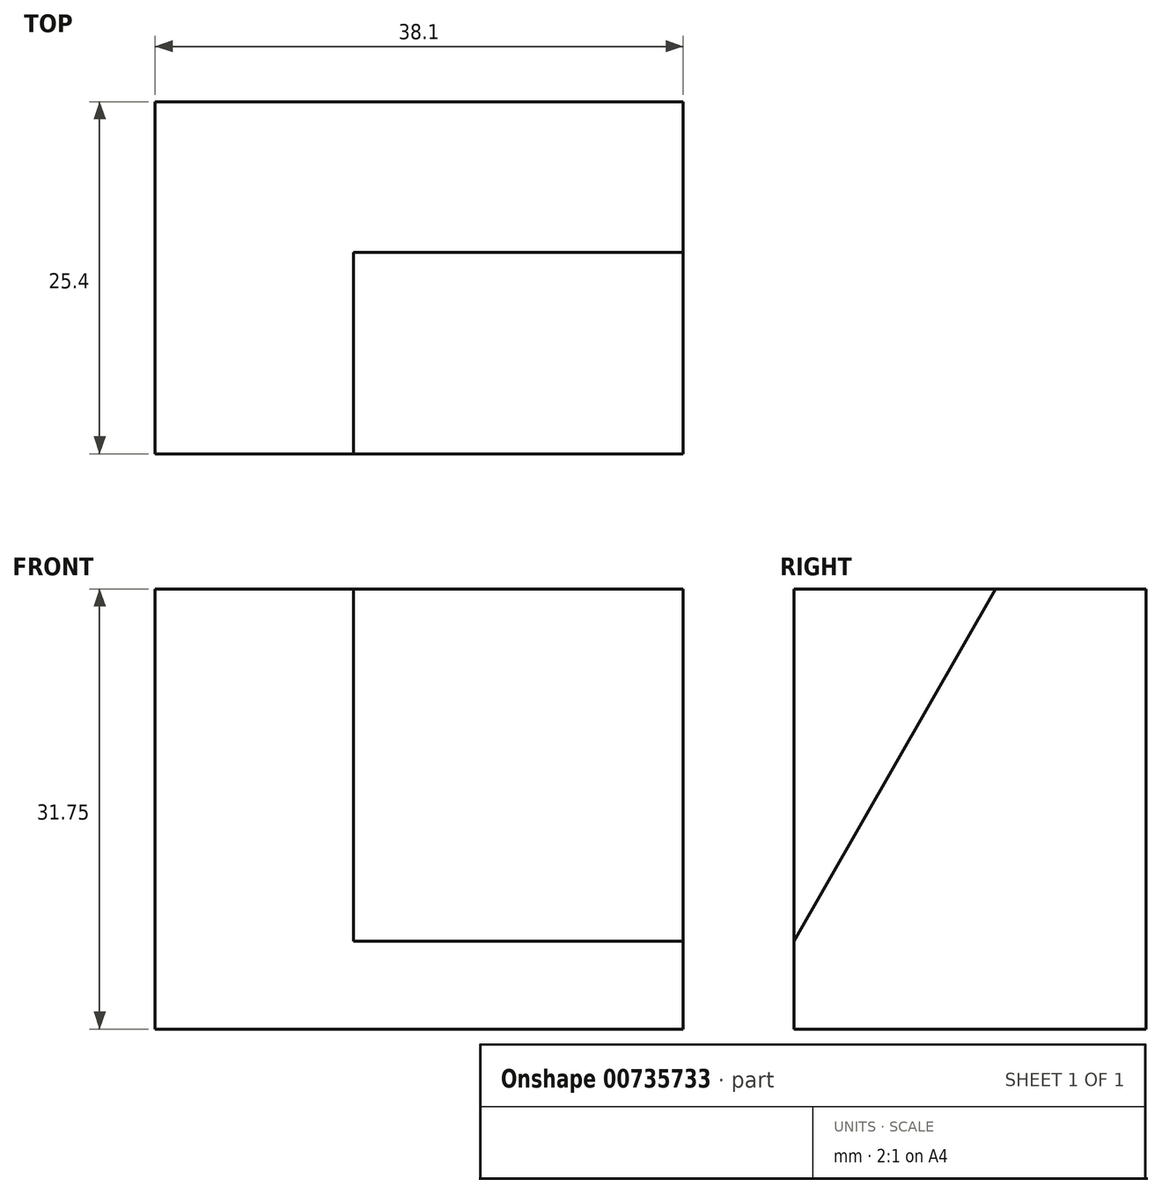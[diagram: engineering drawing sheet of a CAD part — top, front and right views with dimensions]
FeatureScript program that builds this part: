
annotation { "Feature Type Name" : "Feature", "Feature Type Description" : "" }
export const myFeature = defineFeature(function(context is Context, id is Id, definition is map)
    precondition{}
    {
        {
            var Q0;
            Q0=qCreatedBy(makeId("Front.planeOp"),FACE);
            var sketch = newSketch(context, id + "F0", { "sketchPlane" : qUnion([Q0])});
            skLineSegment(sketch, "E0", {"start": v(0, 0) * mm, "end": v(0, 31.75) * mm});
            skLineSegment(sketch, "E1", {"start": v(0, 31.75) * mm, "end": v(38.1, 31.75) * mm});
            skLineSegment(sketch, "E2", {"start": v(38.1, 31.75) * mm, "end": v(38.1, 0) * mm});
            skLineSegment(sketch, "E3", {"start": v(38.1, 0) * mm, "end": v(0, 0) * mm});
            skSolve(sketch);
        }
        {
            var Q0;
            Q0=makeQuery(id+"F0.imprint","IMPRINT",FACE,{"disambiguationData":[TD([[makeQuery(id+"F0.imprint","IMPRINT",EDGE,{"derivedFrom":sQuery(id+"F0.wireOp",EDGE,"E0")}),-1.0]])]});
            extrude(context, id + "F1", {"entities" : qUnion([Q0]), "depth" : 25.4 * mm, "offsetDistance" : 25.4 * mm});
        }
        {
            var Q0;
            Q0=makeQuery(id+"F1.opExtrude","SWEPT_FACE",FACE,{"disambiguationData":[OSD([sQuery(id+"F0.wireOp",EDGE,"E1")])]});
            var sketch = newSketch(context, id + "F2", { "sketchPlane" : qUnion([Q0])});
            skLineSegment(sketch, "E4", {"start": v(14.31, -25.4) * mm, "end": v(14.31, -10.88) * mm});
            skLineSegment(sketch, "E5", {"start": v(14.31, -10.88) * mm, "end": v(38.1, -10.88) * mm});
            skLineSegment(sketch, "E6", {"start": v(38.1, -10.88) * mm, "end": v(38.1, -25.4) * mm});
            skLineSegment(sketch, "E7", {"start": v(38.1, -25.4) * mm, "end": v(14.31, -25.4) * mm});
            skSolve(sketch);
        }
        {
            var Q0;
            Q0=makeQuery(id+"F2.imprint","IMPRINT",FACE,{"disambiguationData":[TD([[makeQuery(id+"F2.imprint","IMPRINT",EDGE,{"derivedFrom":sQuery(id+"F2.wireOp",EDGE,"E4")}),-1.0]])]});
            extrude(context, id + "F3", {"entities" : qUnion([Q0]), "operationType" : NewBodyOperationType.REMOVE, "oppositeDirection" : true, "depth" : 25.4 * mm, "offsetDistance" : 25.4 * mm});
        }
        {
            var Q0;
            Q0=makeQuery(id+"F1.opExtrude","SWEPT_FACE",FACE,{"disambiguationData":[OSD([sQuery(id+"F0.wireOp",EDGE,"E2")])]});
            var sketch = newSketch(context, id + "F4", { "sketchPlane" : qUnion([Q0])});
            skLineSegment(sketch, "E8", {"start": v(-25.4, 6.35) * mm, "end": v(-10.88, 31.75) * mm});
            skLineSegment(sketch, "E9", {"start": v(-10.88, 31.75) * mm, "end": v(-10.88, 6.35) * mm});
            skLineSegment(sketch, "E10", {"start": v(-10.88, 6.35) * mm, "end": v(-25.4, 6.35) * mm});
            skSolve(sketch);
        }
        {
            var Q0;
            Q0=makeQuery(id+"F4.imprint","IMPRINT",FACE,{"disambiguationData":[TD([[makeQuery(id+"F4.imprint","IMPRINT",EDGE,{"derivedFrom":sQuery(id+"F4.wireOp",EDGE,"E8")}),-1.0]])]});
            extrude(context, id + "F5", {"entities" : qUnion([Q0]), "operationType" : NewBodyOperationType.ADD, "oppositeDirection" : true, "depth" : 25.4 * mm, "offsetDistance" : 25.4 * mm});
        }
    });
